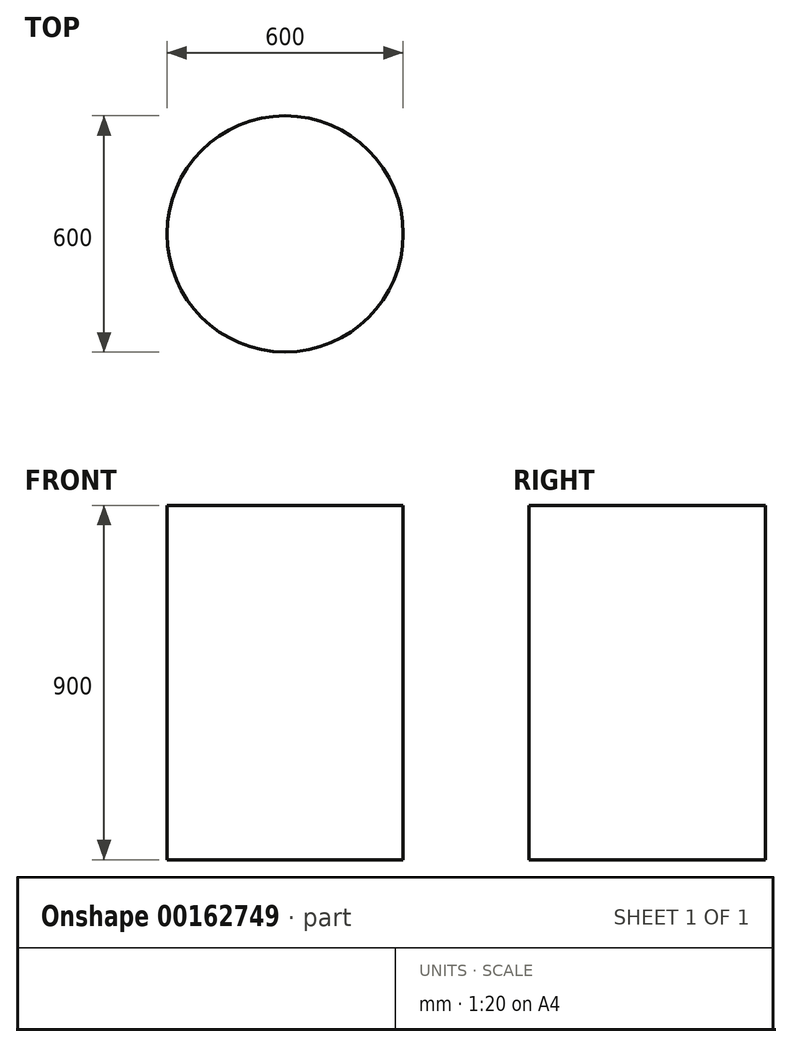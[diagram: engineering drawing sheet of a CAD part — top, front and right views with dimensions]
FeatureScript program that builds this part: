
annotation { "Feature Type Name" : "Feature", "Feature Type Description" : "" }
export const myFeature = defineFeature(function(context is Context, id is Id, definition is map)
    precondition{}
    {
        {
            var Q0;
            Q0=qCreatedBy(makeId("Top.planeOp"),FACE);
            var sketch = newSketch(context, id + "F0", { "sketchPlane" : qUnion([Q0])});
            skCircle(sketch, "E0", {"center": v(0, 0) * mm, "radius": 300 * mm});
            skSolve(sketch);
        }
        {
            var Q0;
            Q0=makeQuery(id+"F0.imprint","IMPRINT",FACE,{"disambiguationData":[TD([[makeQuery(id+"F0.imprint","IMPRINT",EDGE,{"derivedFrom":sQuery(id+"F0.wireOp",EDGE,"E0")}),1.0]])]});
            extrude(context, id + "F1", {"entities" : qUnion([Q0]), "depth" : 900 * mm});
        }
    });
